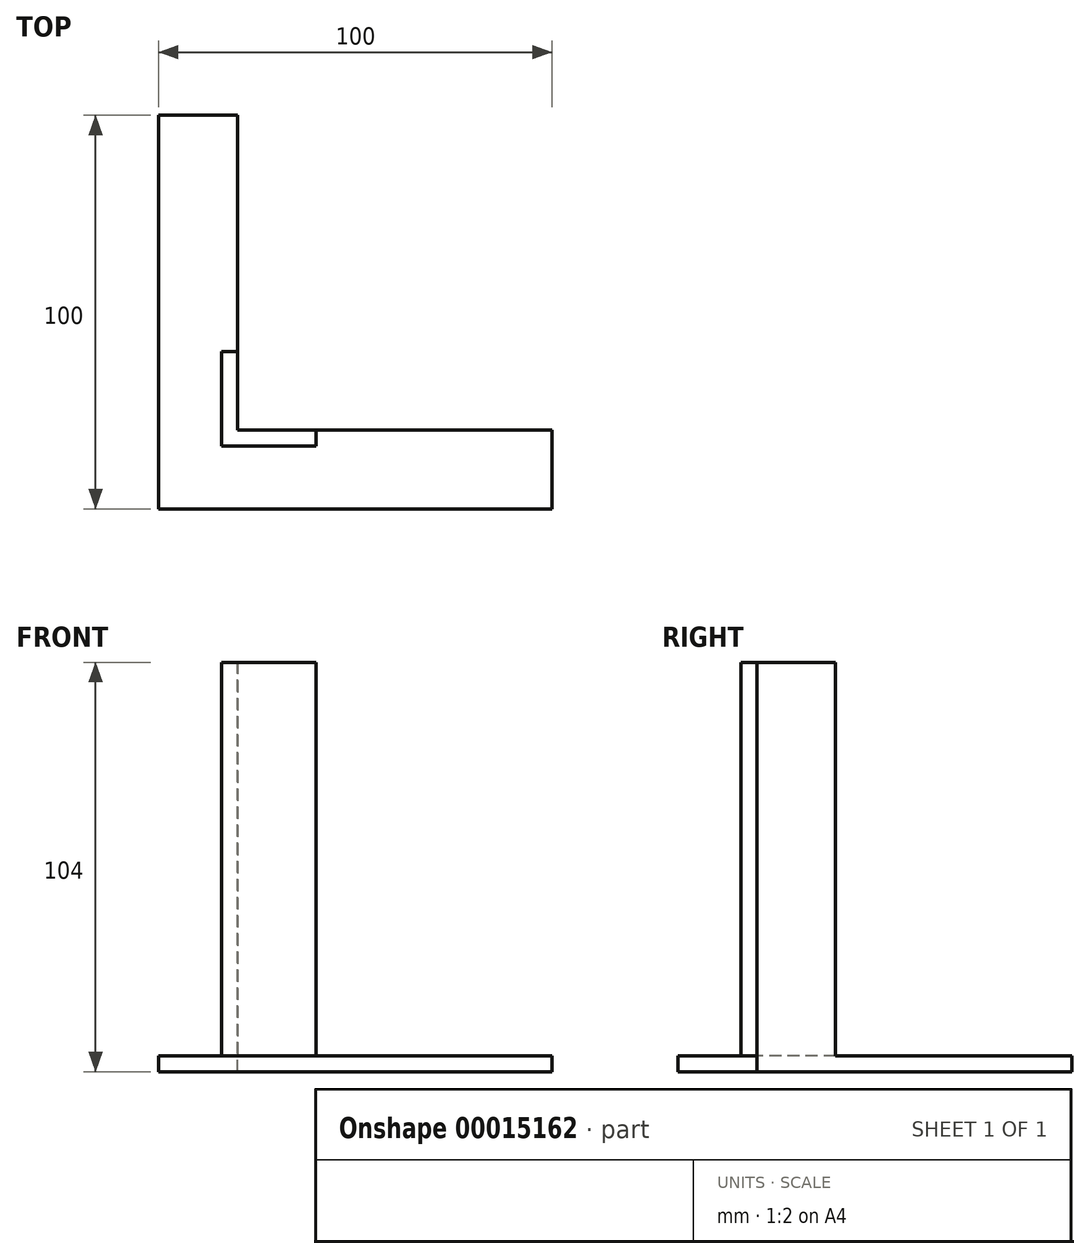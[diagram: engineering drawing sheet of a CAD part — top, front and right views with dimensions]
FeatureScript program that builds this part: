
annotation { "Feature Type Name" : "Feature", "Feature Type Description" : "" }
export const myFeature = defineFeature(function(context is Context, id is Id, definition is map)
    precondition{}
    {
        {
            var Q0;
            Q0=qCreatedBy(makeId("Top.planeOp"),FACE);
            var sketch = newSketch(context, id + "F0", { "sketchPlane" : qUnion([Q0])});
            skLineSegment(sketch, "E0.rect.bottom", {"start": v(50, -50) * mm, "end": v(-50, -50) * mm});
            skLineSegment(sketch, "E0.rect.top", {"start": v(-30, 50) * mm, "end": v(-50, 50) * mm});
            skLineSegment(sketch, "E0.rect.left", {"start": v(50, -50) * mm, "end": v(50, -30) * mm});
            skLineSegment(sketch, "E0.rect.right", {"start": v(-50, -50) * mm, "end": v(-50, 50) * mm});
            skPoint(sketch, "E0.rect.middle", {"position": v(0, 0) * mm});
            skLineSegment(sketch, "E1", {"start": v(-30, 50) * mm, "end": v(-30, -30) * mm});
            skLineSegment(sketch, "E2", {"start": v(-30, -30) * mm, "end": v(50, -30) * mm});
            skLineSegment(sketch, "E3", {"start": v(-30, -10) * mm, "end": v(-34, -10) * mm});
            skLineSegment(sketch, "E4", {"start": v(-34, -10) * mm, "end": v(-34, -34) * mm});
            skLineSegment(sketch, "E5", {"start": v(-34, -34) * mm, "end": v(-10, -34) * mm});
            skLineSegment(sketch, "E6", {"start": v(-10, -34) * mm, "end": v(-10, -30) * mm});
            skSolve(sketch);
        }
        {
            var Q0;
            Q0=makeQuery(id+"F0.imprint","IMPRINT",FACE,{"disambiguationData":[TD([[makeQuery(id+"F0.imprint","IMPRINT",EDGE,{"derivedFrom":sQuery(id+"F0.wireOp",EDGE,"E0.rect.bottom")}),-1.0]])]});
            var Q1;
            {var subQ1=sQuery(id+"F0.wireOp",EDGE,"E3");Q1=makeQuery(id+"F0.imprint","IMPRINT",FACE,{"disambiguationData":[TD([[makeQuery(id+"F0.imprint","IMPRINT",EDGE,{"derivedFrom":subQ1}),1.0]])]});}
            extrude(context, id + "F1", {"entities" : qUnion([Q0, Q1]), "oppositeDirection" : true, "depth" : 4 * mm});
        }
        {
            var Q0;
            {var subQ1=sQuery(id+"F0.wireOp",EDGE,"E3");Q0=makeQuery(id+"F0.imprint","IMPRINT",FACE,{"disambiguationData":[TD([[makeQuery(id+"F0.imprint","IMPRINT",EDGE,{"derivedFrom":subQ1}),1.0]])]});}
            extrude(context, id + "F2", {"entities" : qUnion([Q0]), "operationType" : NewBodyOperationType.ADD, "depth" : 100 * mm});
        }
    });
